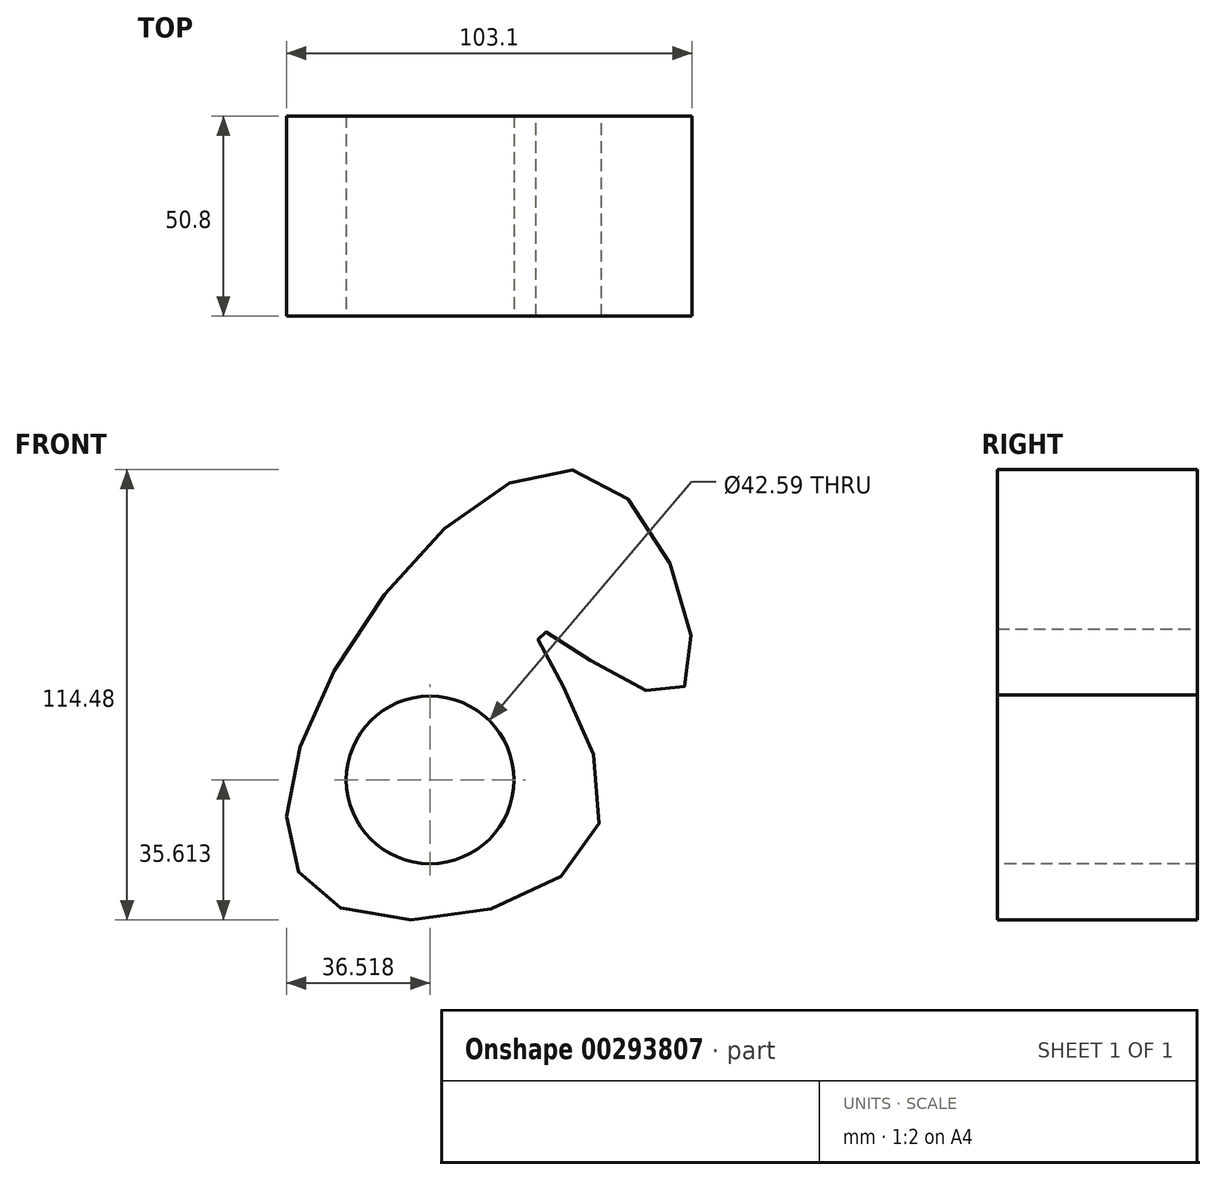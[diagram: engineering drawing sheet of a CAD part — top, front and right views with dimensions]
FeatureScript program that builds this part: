
annotation { "Feature Type Name" : "Feature", "Feature Type Description" : "" }
export const myFeature = defineFeature(function(context is Context, id is Id, definition is map)
    precondition{}
    {
        {
            var Q0;
            Q0=qCreatedBy(makeId("Front.planeOp"),FACE);
            var sketch = newSketch(context, id + "F0", { "sketchPlane" : qUnion([Q0])});
            skFitSpline(sketch, "E0", {"points": [v(-51.55, 15.64) * mm, v(-52.45, -43.4) * mm, v(15.83, -22.79) * mm, v(0, 26.2) * mm, v(35.27, 9.96) * mm, v(17.18, 63.97) * mm, v(-51.55, 15.64) * mm]});
            skSolve(sketch);
        }
        {
            var Q0;
            Q0=makeQuery(id+"F0.imprint","IMPRINT",FACE,{"disambiguationData":[TD([[makeQuery(id+"F0.imprint","IMPRINT",EDGE,{"derivedFrom":sQuery(id+"F0.wireOp",EDGE,"E0")}),1.0]])]});
            extrude(context, id + "F1", {"entities" : qUnion([Q0]), "depth" : 50.8 * mm});
        }
        {
            var Q0;
            Q0=makeQuery(id+"F1.opExtrude","CAP_FACE",FACE,{"disambiguationData":[OSD([sQuery(id+"F0.wireOp",EDGE,"E0")])],"isStart":false});
            var sketch = newSketch(context, id + "F2", { "sketchPlane" : qUnion([Q0])});
            skCircle(sketch, "E1", {"center": v(-27.2, -12.07) * mm, "radius": 21.3 * mm});
            skSolve(sketch);
        }
        {
            var Q0;
            Q0=makeQuery(id+"F2.imprint","IMPRINT",FACE,{"disambiguationData":[TD([[makeQuery(id+"F2.imprint","IMPRINT",EDGE,{"derivedFrom":sQuery(id+"F2.wireOp",EDGE,"E1")}),1.0]])]});
            extrude(context, id + "F3", {"entities" : qUnion([Q0]), "operationType" : NewBodyOperationType.REMOVE, "endBound" : BoundingType.THROUGH_ALL, "oppositeDirection" : true, "depth" : 25.4 * mm});
        }
    });
